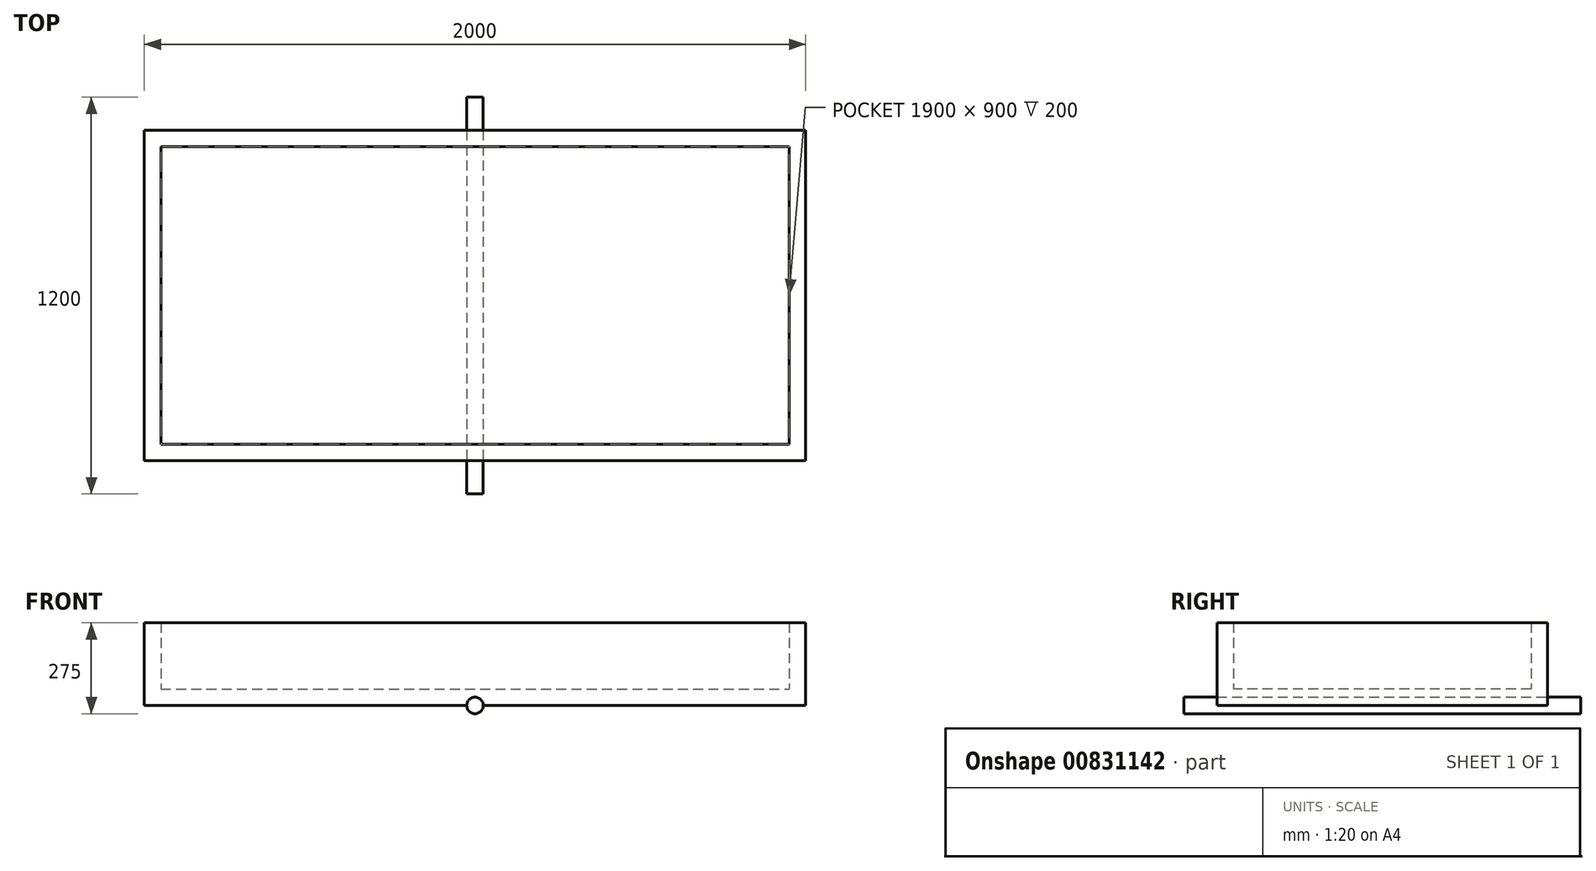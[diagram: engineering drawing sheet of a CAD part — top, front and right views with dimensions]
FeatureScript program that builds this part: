
annotation { "Feature Type Name" : "Feature", "Feature Type Description" : "" }
export const myFeature = defineFeature(function(context is Context, id is Id, definition is map)
    precondition{}
    {
        {
            var Q0;
            Q0=qCreatedBy(makeId("Top.planeOp"),FACE);
            var sketch = newSketch(context, id + "F0", { "sketchPlane" : qUnion([Q0])});
            skLineSegment(sketch, "E0.bottom", {"start": v(-1000, 500) * mm, "end": v(1000, 500) * mm});
            skLineSegment(sketch, "E0.top", {"start": v(-1000, -500) * mm, "end": v(1000, -500) * mm});
            skLineSegment(sketch, "E0.left", {"start": v(-1000, 500) * mm, "end": v(-1000, -500) * mm});
            skLineSegment(sketch, "E0.right", {"start": v(1000, 500) * mm, "end": v(1000, -500) * mm});
            skPoint(sketch, "E0.middle", {"position": v(0, 0) * mm});
            skSolve(sketch);
        }
        {
            var Q0;
            Q0 = qSketchRegion(id + "F0", true);
            extrude(context, id + "F1", {"entities" : qUnion([Q0]), "depth" : 250 * mm, "offsetDistance" : 25 * mm});
        }
        {
            var Q0;
            Q0=makeQuery(id+"F1.opExtrude","CAP_FACE",FACE,{"disambiguationData":[OSD([sQuery(id+"F0.wireOp",EDGE,"E0.bottom"),sQuery(id+"F0.wireOp",EDGE,"E0.top"),sQuery(id+"F0.wireOp",EDGE,"E0.left"),sQuery(id+"F0.wireOp",EDGE,"E0.right")])],"isStart":false});
            shell(context, id + "F2", {"entities" : qUnion([Q0]), "thickness" : 50 * mm});
        }
        {
            var Q0;
            Q0=qCreatedBy(makeId("Front.planeOp"),FACE);
            var sketch = newSketch(context, id + "F3", { "sketchPlane" : qUnion([Q0])});
            skCircle(sketch, "E1", {"center": v(0, 0) * mm, "radius": 25 * mm});
            skSolve(sketch);
        }
        {
            var Q0;
            Q0 = qSketchRegion(id + "F3", true);
            extrude(context, id + "F4", {"entities" : qUnion([Q0]), "operationType" : NewBodyOperationType.REMOVE, "endBound" : BoundingType.THROUGH_ALL, "oppositeDirection" : true, "depth" : 25 * mm, "offsetDistance" : 25 * mm, "hasSecondDirection" : true, "secondDirectionBound" : SecondDirectionBoundingType.THROUGH_ALL, "secondDirectionOppositeDirection" : false, "secondDirectionDepth" : 25 * mm});
        }
        {
            var Q0;
            Q0 = qSketchRegion(id + "F3", true);
            extrude(context, id + "F5", {"entities" : qUnion([Q0]), "depth" : 600 * mm, "offsetDistance" : 25 * mm, "hasSecondDirection" : true, "secondDirectionOppositeDirection" : true, "secondDirectionDepth" : 600 * mm});
        }
    });
